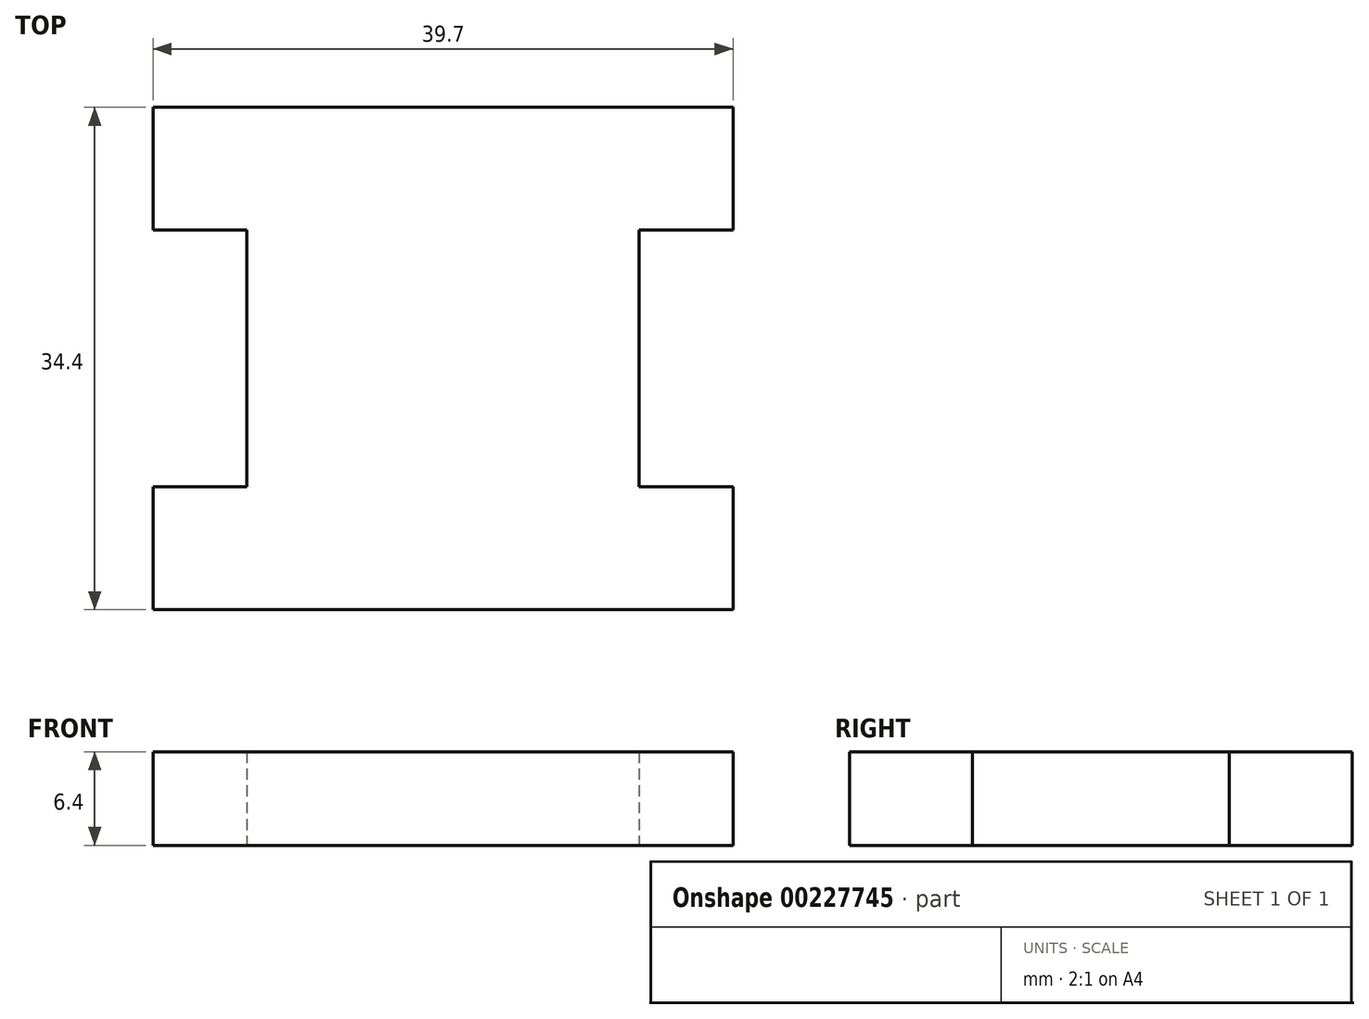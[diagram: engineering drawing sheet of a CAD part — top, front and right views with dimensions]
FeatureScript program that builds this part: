
annotation { "Feature Type Name" : "Feature", "Feature Type Description" : "" }
export const myFeature = defineFeature(function(context is Context, id is Id, definition is map)
    precondition{}
    {
        {
            var Q0;
            Q0=qCreatedBy(makeId("Top.planeOp"),FACE);
            var sketch = newSketch(context, id + "F0", { "sketchPlane" : qUnion([Q0])});
            skPoint(sketch, "E0.0", {"position": v(-19.85, 17.2) * mm});
            skPoint(sketch, "E0.1", {"position": v(-19.85, 8.8) * mm});
            skPoint(sketch, "E0.2", {"position": v(-13.43, 8.8) * mm});
            skPoint(sketch, "E0.9", {"position": v(13.43, 8.8) * mm});
            skPoint(sketch, "E0.10", {"position": v(19.85, 8.8) * mm});
            skPoint(sketch, "E0.11", {"position": v(19.85, 17.2) * mm});
            skLineSegment(sketch, "E1", {"start": v(-19.85, 17.2) * mm, "end": v(19.85, 17.2) * mm});
            skLineSegment(sketch, "E2", {"start": v(19.85, 8.8) * mm, "end": v(13.43, 8.8) * mm});
            skLineSegment(sketch, "E3", {"start": v(19.85, 17.2) * mm, "end": v(19.85, 8.8) * mm});
            skLineSegment(sketch, "E4", {"start": v(13.43, 8.8) * mm, "end": v(13.43, 0) * mm});
            skLineSegment(sketch, "E5", {"start": v(-13.43, 0) * mm, "end": v(-13.43, 8.8) * mm});
            skLineSegment(sketch, "E6", {"start": v(-13.42, 8.8) * mm, "end": v(-19.85, 8.8) * mm});
            skLineSegment(sketch, "E7", {"start": v(-19.85, 8.8) * mm, "end": v(-19.85, 17.2) * mm});
            skPoint(sketch, "E8", {"position": v(-13.43, 0) * mm});
            skPoint(sketch, "E9", {"position": v(13.43, 0) * mm});
            skLineSegment(sketch, "E10", {"start": v(-13.43, 0) * mm, "end": v(13.43, 0) * mm, "construction": true});
            skPoint(sketch, "E11", {"position": v(0, 0) * mm});
            skPoint(sketch, "E12.MirrorP", {"position": v(-19.85, -17.2) * mm});
            skPoint(sketch, "E13.MirrorP", {"position": v(13.42, -8.8) * mm});
            skPoint(sketch, "E14.MirrorP", {"position": v(19.85, -8.8) * mm});
            skLineSegment(sketch, "E15.MirrorCS", {"start": v(19.85, -17.2) * mm, "end": v(19.85, -8.8) * mm});
            skLineSegment(sketch, "E16.MirrorCS", {"start": v(-19.85, -17.2) * mm, "end": v(19.85, -17.2) * mm});
            skLineSegment(sketch, "E17.MirrorCS", {"start": v(-13.43, -8.8) * mm, "end": v(-19.85, -8.8) * mm});
            skPoint(sketch, "E18.MirrorP", {"position": v(-19.85, -8.8) * mm});
            skPoint(sketch, "E19.MirrorP", {"position": v(-13.43, -8.8) * mm});
            skLineSegment(sketch, "E20.MirrorCS", {"start": v(19.85, -8.8) * mm, "end": v(13.42, -8.8) * mm});
            skLineSegment(sketch, "E21.MirrorCS", {"start": v(-19.85, -8.8) * mm, "end": v(-19.85, -17.2) * mm});
            skPoint(sketch, "E22.MirrorP", {"position": v(19.85, -17.2) * mm});
            skLineSegment(sketch, "E23.MirrorCS", {"start": v(13.42, -8.8) * mm, "end": v(13.43, 0) * mm});
            skLineSegment(sketch, "E24.MirrorCS", {"start": v(-13.43, 0) * mm, "end": v(-13.43, -8.8) * mm});
            skSolve(sketch);
        }
        {
            var Q0;
            Q0=makeQuery(id+"F0.imprint","IMPRINT",FACE,{"disambiguationData":[TD([[makeQuery(id+"F0.imprint","IMPRINT",EDGE,{"derivedFrom":sQuery(id+"F0.wireOp",EDGE,"E1")}),-1.0]])]});
            extrude(context, id + "F1", {"entities" : qUnion([Q0]), "flatOperationType" : FlatOperationType.REMOVE, "depth" : 6.4 * mm, "offsetDistance" : 25 * mm, "domain" : OperationDomain.MODEL});
        }
    });
